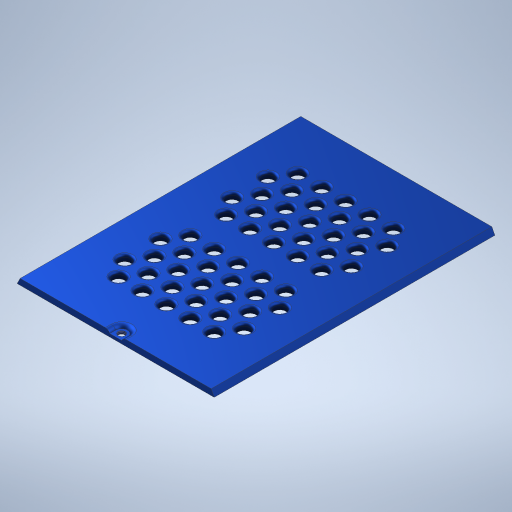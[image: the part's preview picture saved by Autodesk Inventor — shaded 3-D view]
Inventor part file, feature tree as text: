
AUTODESK INVENTOR PART (.ipt)
format: ipt  version: 2023 (Build 270158000, 158)  size: 583,168 bytes
history: native  units: mm
features: extrude x4, sketch x3, fillet x2, thread x1
ambient origin geometry x8: Origin, YZ Plane, XZ Plane, XY Plane, X Axis, Y Axis, Z Axis, Center Point
bodies: Solid1 (feature_tree)
feature tree (10):
  extrude  "Extrusion1"  Depth=80.0mm
  sketch  "Sketch2"  dims[d1=82.5mm d2=80.0mm]
  extrude  "Extrusion2"  Depth=41.25mm
  extrude  "Extrusion3"  Depth=1.25mm
  sketch  "Sketch3"  dims[d3=40.0mm d4=41.25mm]
  extrude  "Extrusion4"  Depth=117.483mm TaperAngle=0.0deg
  fillet  "Fillet2"  Radius=3.0mm
  fillet  "Fillet3"  Radius=2.5mm
  thread  "Thread1"  [1 undecoded]
  sketch  "Sketch4"  dims[d5=2.5mm d6=1.25mm d7=117.483mm d8=0.0mm d9=3.0mm d10=2.5mm d11=0.0mm d12=0.0mm d13=5.0mm d14=1.25mm d15=0.0mm d17=5.0mm d18=21.25mm d19=50.0mm d21=10.0mm d22=10.0mm d24=10.0mm d26=7.5mm d27=5.0mm d28=60.0mm d30=10.0mm d31=10.0mm d33=10.0mm d35=16.25mm d37=50.0mm d38=82.5mm d39=21.25mm d40=40.0mm d41=60.0mm d42=90.0deg d43=60.0mm d45=15.0mm d46=10.0mm d48=10.0mm d50=21.233mm d51=10.0mm d52=0.0mm d53=1.0mm d54=2.0mm d56=1.5mm d57=90.0deg d58=0.0mm d59=40.0mm d61=80.0mm d62=9.0mm d63=0.0mm d16=0.0mm d60=0.872665mm]
note: 1 required parameter value undecoded (feature->parameter linkage not recoverable at this tier; creation-order binding heuristic only, values carry confidence <= 0.55)
